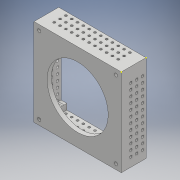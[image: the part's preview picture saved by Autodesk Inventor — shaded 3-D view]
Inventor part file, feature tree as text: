
AUTODESK INVENTOR PART (.ipt)
format: ipt  version: 2018 (Build 220112000, 112)  size: 306,688 bytes
history: native  units: mm
features: sketch x9, extrude x7, pattern_linear x4
ambient origin geometry x8: Origin, YZ Plane, XZ Plane, XY Plane, X Axis, Y Axis, Z Axis, Center Point
bodies: Solid1 (feature_tree)
feature tree (20):
  sketch  "Sketch1"  dims[d0=150.0mm d1=150.0mm]
  extrude  "Extrusion1"  Depth=150.0mm
  extrude  "Extrusion2"  Depth=7.5mm TaperAngle=0.0deg
  extrude  "Extrusion3"  Depth=35.0mm TaperAngle=0.0deg
  extrude  "Extrusion4"  Depth=10.0mm
  pattern_linear  "Rectangular Pattern1"  Count1=2 Spacing1=132.0mm
  extrude  "Extrusion5"  Depth=132.0mm
  pattern_linear  "Rectangular Pattern2"  Count1=8 Spacing1=0.0mm
  extrude  "Extrusion6"  Depth=132.0mm
  pattern_linear  "Rectangular Pattern3"  Count1=30 Spacing1=0.0mm
  extrude  "Extrusion7"  Depth=10.0mm
  pattern_linear  "Rectangular Pattern4"  Count1=30 Spacing1=0.0mm
  sketch  "Sketch9"  dims[d39=120.0mm d41=10.0mm d42=30.0mm d44=10.0mm]
  sketch  "Sketch2"  dims[d2=7.5mm d3=0.0mm d5=7.5mm d6=0.0mm]
  sketch  "Sketch3"  dims[d7=4.0mm d8=35.0mm d9=0.0mm]
  sketch  "Sketch4"  dims[d10=10.0mm d11=10.0mm]
  sketch  "Sketch5"  dims[d12=35.0mm d13=0.0mm d14=20.0mm d16=132.0mm]
  sketch  "Sketch6"  dims[d17=20.0mm d19=132.0mm d20=5.5mm d21=80.0mm d22=0.0mm]
  sketch  "Sketch7"  dims[d23=20.0mm d25=132.0mm d26=20.0mm d28=132.0mm d29=300.0mm d30=0.0mm]
  sketch  "Sketch8"  dims[d31=120.0mm d33=10.0mm d34=30.0mm d36=10.0mm d37=300.0mm d38=0.0mm]
